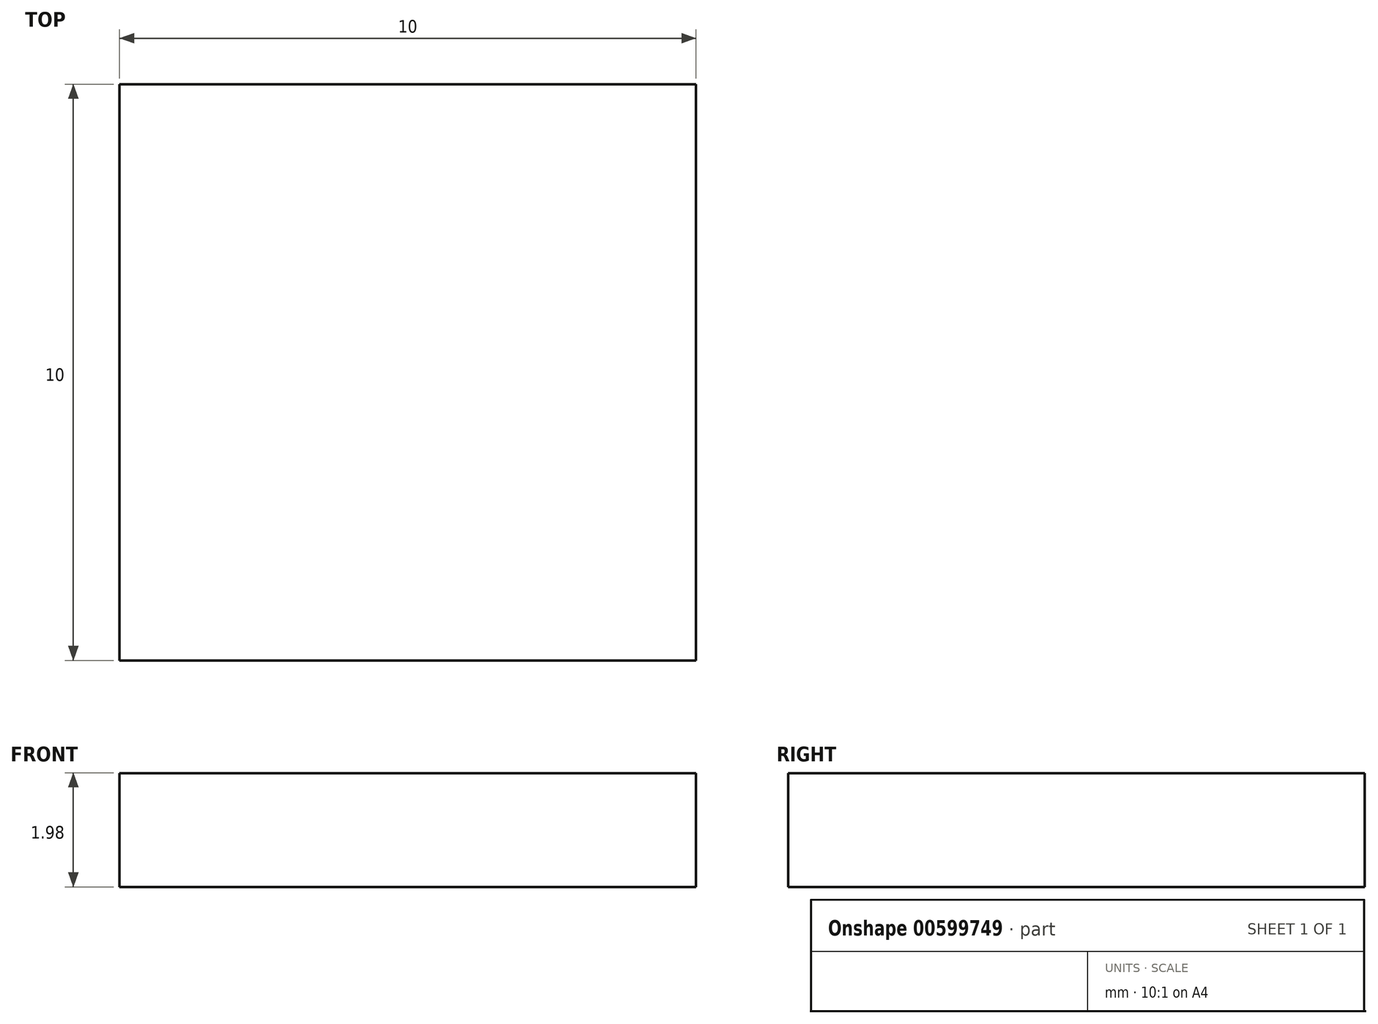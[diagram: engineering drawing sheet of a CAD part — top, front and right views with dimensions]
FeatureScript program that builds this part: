
annotation { "Feature Type Name" : "Feature", "Feature Type Description" : "" }
export const myFeature = defineFeature(function(context is Context, id is Id, definition is map)
    precondition{}
    {
        {
            var Q0;
            Q0=qCreatedBy(makeId("Top.planeOp"),FACE);
            var sketch = newSketch(context, id + "F0", { "sketchPlane" : qUnion([Q0])});
            skLineSegment(sketch, "E0.bottom", {"start": v(5, 5) * mm, "end": v(-5, 5) * mm});
            skLineSegment(sketch, "E0.top", {"start": v(5, -5) * mm, "end": v(-5, -5) * mm});
            skLineSegment(sketch, "E0.left", {"start": v(5, 5) * mm, "end": v(5, -5) * mm});
            skLineSegment(sketch, "E0.right", {"start": v(-5, 5) * mm, "end": v(-5, -5) * mm});
            skPoint(sketch, "E0.middle", {"position": v(0, 0) * mm});
            skSolve(sketch);
        }
        {
            var Q0;
            Q0=makeQuery(id+"F0.imprint","IMPRINT",FACE,{"disambiguationData":[TD([[makeQuery(id+"F0.imprint","IMPRINT",EDGE,{"derivedFrom":sQuery(id+"F0.wireOp",EDGE,"E0.bottom")}),1.0]])]});
            extrude(context, id + "F1", {"entities" : qUnion([Q0]), "depth" : 1.98 * mm, "offsetDistance" : 25 * mm});
        }
    });
